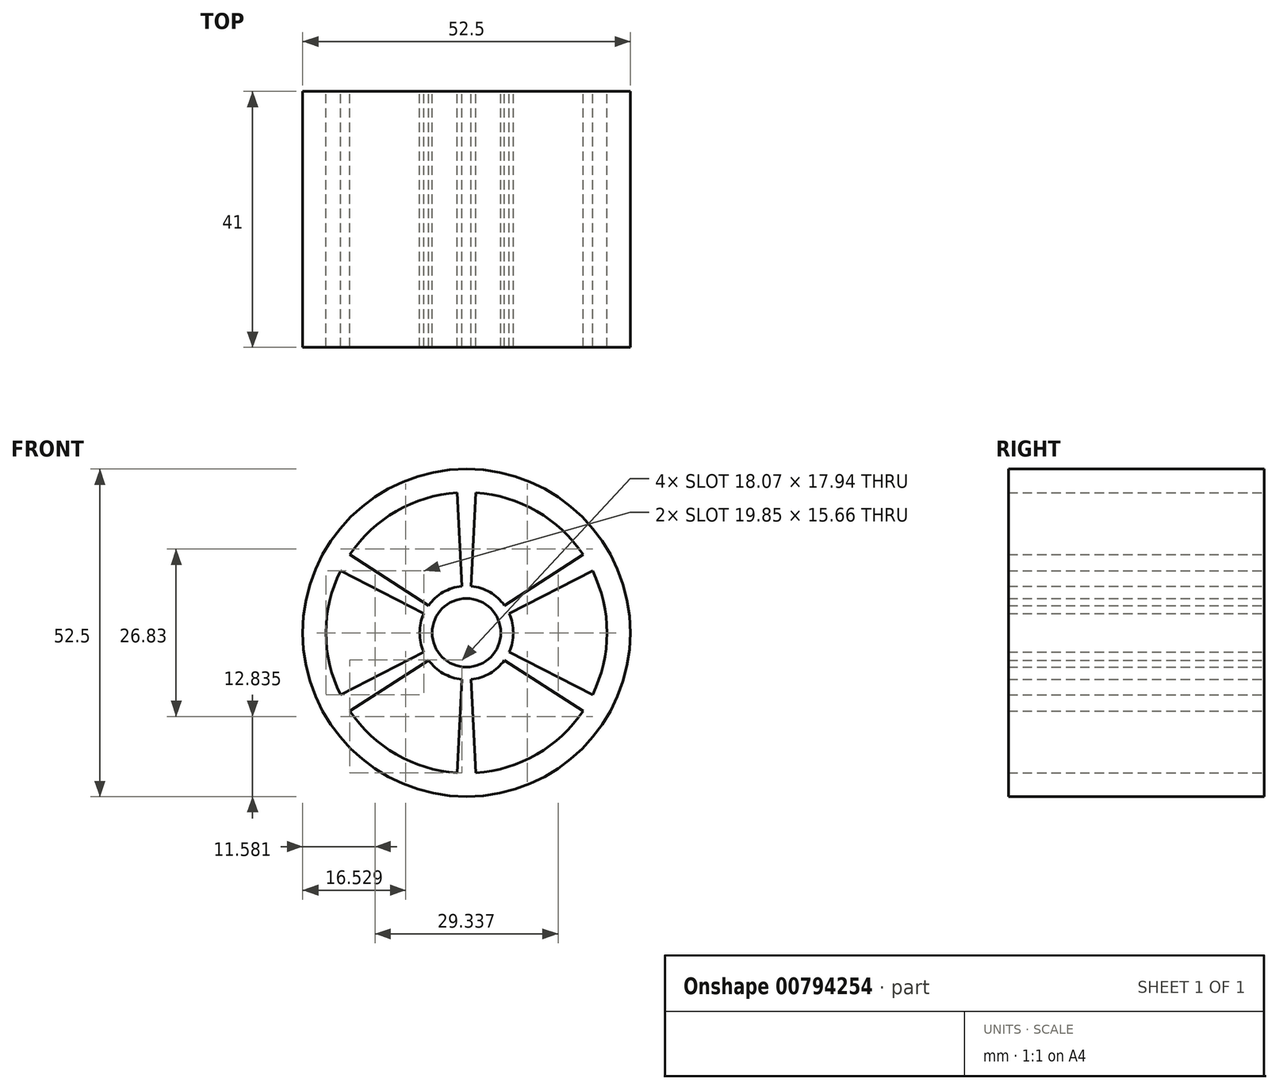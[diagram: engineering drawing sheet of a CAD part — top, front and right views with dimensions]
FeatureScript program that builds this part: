
annotation { "Feature Type Name" : "Feature", "Feature Type Description" : "" }
export const myFeature = defineFeature(function(context is Context, id is Id, definition is map)
    precondition{}
    {
        {
            var Q0;
            Q0=qCreatedBy(makeId("Front.planeOp"),FACE);
            var sketch = newSketch(context, id + "F0", { "sketchPlane" : qUnion([Q0])});
            skCircle(sketch, "E0", {"center": v(0, 0) * mm, "radius": 26.25 * mm});
            skArc(sketch, "E1", {"start": v(-3.35, 4.36) * mm, "mid": v(2.77, -4.75) * mm, "end": v(-2.15, 5.06) * mm});
            skLineSegment(sketch, "E2", {"start": v(1.5, 22.45) * mm, "end": v(0.75, 7.46) * mm});
            skLineSegment(sketch, "E3", {"start": v(-1.5, 22.45) * mm, "end": v(-0.75, 7.46) * mm});
            skPoint(sketch, "E4.end.orphan", {"position": v(0, 22.5) * mm});
            skPoint(sketch, "E4.start.orphan", {"position": v(0, 7.5) * mm});
            skLineSegment(sketch, "E5.anchor1", {"start": v(0, 0) * mm, "end": v(0.75, 7.46) * mm, "construction": true});
            skLineSegment(sketch, "E5.anchor2", {"start": v(0, 0) * mm, "end": v(0.75, 7.46) * mm, "construction": true});
            skLineSegment(sketch, "E6.1.0", {"start": v(-20.2, 9.93) * mm, "end": v(-6.84, 3.08) * mm});
            skLineSegment(sketch, "E6.1.1", {"start": v(-18.7, 12.52) * mm, "end": v(-6.09, 4.38) * mm});
            skLineSegment(sketch, "E6.2.0", {"start": v(-18.7, -12.52) * mm, "end": v(-6.09, -4.38) * mm});
            skLineSegment(sketch, "E6.2.1", {"start": v(-20.2, -9.93) * mm, "end": v(-6.84, -3.08) * mm});
            skLineSegment(sketch, "E6.3.0", {"start": v(1.5, -22.45) * mm, "end": v(0.75, -7.46) * mm});
            skLineSegment(sketch, "E6.3.1", {"start": v(-1.5, -22.45) * mm, "end": v(-0.75, -7.46) * mm});
            skLineSegment(sketch, "E6.4.0", {"start": v(20.2, -9.93) * mm, "end": v(6.84, -3.08) * mm});
            skLineSegment(sketch, "E6.4.1", {"start": v(18.7, -12.52) * mm, "end": v(6.09, -4.38) * mm});
            skLineSegment(sketch, "E6.5.0", {"start": v(18.7, 12.52) * mm, "end": v(6.09, 4.38) * mm});
            skLineSegment(sketch, "E6.5.1", {"start": v(20.2, 9.93) * mm, "end": v(6.84, 3.08) * mm});
            skArc(sketch, "E7.trimOffspring", {"start": v(-20.2, 9.93) * mm, "mid": v(-22.5, 0) * mm, "end": v(-20.2, -9.93) * mm});
            skArc(sketch, "E8.trimOffspring", {"start": v(-18.7, -12.52) * mm, "mid": v(-11.25, -19.49) * mm, "end": v(-1.5, -22.45) * mm});
            skArc(sketch, "E9.trimOffspring", {"start": v(20.2, -9.93) * mm, "mid": v(22.5, 0) * mm, "end": v(20.2, 9.93) * mm});
            skArc(sketch, "E10.trimOffspring", {"start": v(1.5, -22.45) * mm, "mid": v(11.25, -19.49) * mm, "end": v(18.7, -12.52) * mm});
            skArc(sketch, "E11.trimOffspring", {"start": v(-6.09, -4.38) * mm, "mid": v(-3.75, -6.5) * mm, "end": v(-0.75, -7.46) * mm});
            skArc(sketch, "E12.trimOffspring", {"start": v(0.75, -7.46) * mm, "mid": v(3.75, -6.5) * mm, "end": v(6.09, -4.38) * mm});
            skArc(sketch, "E13.trimOffspring", {"start": v(6.84, -3.08) * mm, "mid": v(7.5, 0) * mm, "end": v(6.84, 3.08) * mm});
            skArc(sketch, "E14.trimOffspring", {"start": v(6.09, 4.38) * mm, "mid": v(3.75, 6.5) * mm, "end": v(0.75, 7.46) * mm});
            skArc(sketch, "E15", {"start": v(-18.7, 12.52) * mm, "mid": v(-11.25, 19.49) * mm, "end": v(-1.5, 22.45) * mm});
            skArc(sketch, "E16", {"start": v(1.5, 22.45) * mm, "mid": v(11.25, 19.49) * mm, "end": v(18.7, 12.52) * mm});
            skArc(sketch, "E17", {"start": v(-0.75, 7.46) * mm, "mid": v(-1.74, 7.3) * mm, "end": v(-2.7, 7) * mm});
            skArc(sketch, "E18", {"start": v(-6.84, -3.08) * mm, "mid": v(-7.5, 0) * mm, "end": v(-6.84, 3.08) * mm});
            skLineSegment(sketch, "E19", {"start": v(-9.01, 6.27) * mm, "end": v(-4.4, 3.3) * mm, "construction": true});
            skLineSegment(sketch, "E20", {"start": v(-0.94, 11.28) * mm, "end": v(-0.65, 5.46) * mm, "construction": true});
            skArc(sketch, "E21.trimOffspring", {"start": v(-4.71, 5.83) * mm, "mid": v(-5.45, 5.15) * mm, "end": v(-6.09, 4.38) * mm});
            skArc(sketch, "E22", {"start": v(-4.71, 5.83) * mm, "mid": v(-3.75, 6.5) * mm, "end": v(-2.7, 7) * mm});
            skArc(sketch, "E23", {"start": v(-3.35, 4.36) * mm, "mid": v(-2.77, 4.75) * mm, "end": v(-2.15, 5.06) * mm});
            skSolve(sketch);
        }
        {
            var Q0;
            Q0=makeQuery(id+"F0.imprint","IMPRINT",FACE,{"disambiguationData":[TD([[makeQuery(id+"F0.imprint","IMPRINT",EDGE,{"derivedFrom":sQuery(id+"F0.wireOp",EDGE,"E0")}),1.0]])]});
            extrude(context, id + "F1", {"entities" : qUnion([Q0]), "depth" : 41 * mm, "offsetDistance" : 25 * mm});
        }
    });
